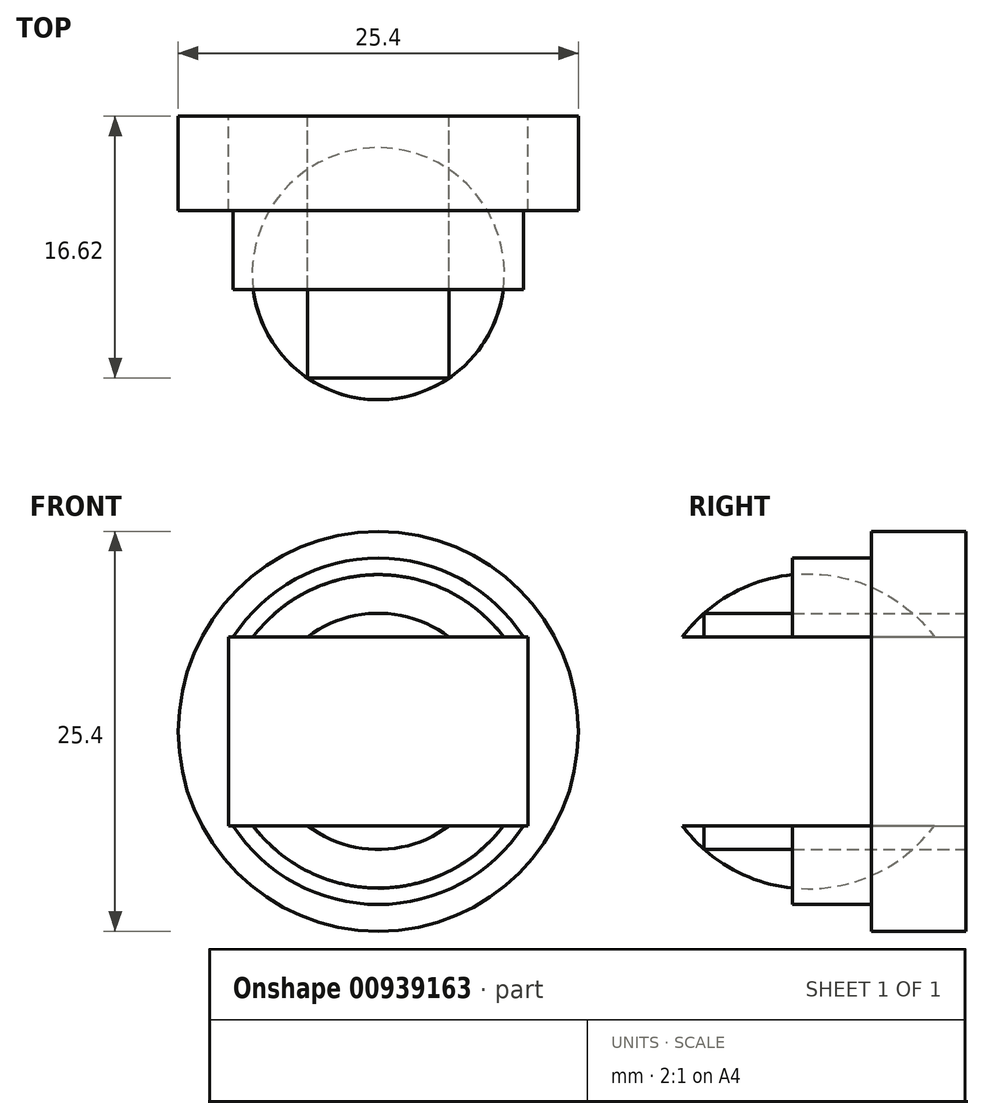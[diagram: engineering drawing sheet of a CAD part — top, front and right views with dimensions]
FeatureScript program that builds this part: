
annotation { "Feature Type Name" : "Feature", "Feature Type Description" : "" }
export const myFeature = defineFeature(function(context is Context, id is Id, definition is map)
    precondition{}
    {
        {
            var Q0;
            Q0=qCreatedBy(makeId("Front.planeOp"),FACE);
            var sketch = newSketch(context, id + "F0", { "sketchPlane" : qUnion([Q0])});
            skCircle(sketch, "E0", {"center": v(0, 0) * mm, "radius": 12.7 * mm});
            skSolve(sketch);
        }
        {
            var Q0;
            Q0=makeQuery(id+"F0.imprint","IMPRINT",FACE,{"disambiguationData":[TD([[makeQuery(id+"F0.imprint","IMPRINT",EDGE,{"derivedFrom":sQuery(id+"F0.wireOp",EDGE,"E0")}),1.0]])]});
            extrude(context, id + "F1", {"entities" : qUnion([Q0]), "depth" : 6 * mm, "offsetDistance" : 25 * mm});
        }
        {
            var Q0;
            Q0=qCreatedBy(makeId("Right.planeOp"),FACE);
            var sketch = newSketch(context, id + "F2", { "sketchPlane" : qUnion([Q0])});
            skArc(sketch, "E1", {"start": v(-10, -10) * mm, "mid": v(0, 0) * mm, "end": v(-10, 10) * mm});
            skLineSegment(sketch, "E2", {"start": v(-10, -10) * mm, "end": v(-10, 10) * mm, "construction": true});
            skLineSegment(sketch, "E3", {"start": v(-10, 10) * mm, "end": v(-10, -10) * mm});
            skSolve(sketch);
        }
        {
            var Q0;
            Q0=makeQuery(id+"F2.imprint","IMPRINT",FACE,{"disambiguationData":[TD([[makeQuery(id+"F2.imprint","IMPRINT",EDGE,{"derivedFrom":sQuery(id+"F2.wireOp",EDGE,"E1")}),1.0]])]});
            var Q1;
            Q1=sQuery(id+"F2.wireOp",EDGE,"E3");
            revolve(context, id + "F3", {"surfaceOperationType" : NewSurfaceOperationType.ADD, "entities" : qUnion([Q0]), "axis" : qUnion([Q1]), "revolveType" : RevolveType.FULL});
        }
        {
            var Q0;
            Q0=makeQuery(id+"F1.opExtrude","CAP_FACE",FACE,{"disambiguationData":[OSD([sQuery(id+"F0.wireOp",EDGE,"E0")])],"isStart":true});
            var sketch = newSketch(context, id + "F4", { "sketchPlane" : qUnion([Q0])});
            skCircle(sketch, "E4", {"center": v(0, 0) * mm, "radius": 7.5 * mm});
            skLineSegment(sketch, "E5.bottom", {"start": v(-9.5, 6) * mm, "end": v(9.5, 6) * mm});
            skLineSegment(sketch, "E5.top", {"start": v(-9.5, -6) * mm, "end": v(9.5, -6) * mm});
            skLineSegment(sketch, "E5.left", {"start": v(-9.5, 6) * mm, "end": v(-9.5, -6) * mm});
            skLineSegment(sketch, "E5.right", {"start": v(9.5, 6) * mm, "end": v(9.5, -6) * mm});
            skSolve(sketch);
        }
        {
            var Q0;
            {var subQ0=sQuery(id+"F4.wireOp",EDGE,"E5.bottom");var subQ1=sQuery(id+"F4.wireOp",EDGE,"E4");var subQ2=makeQuery(id+"F4.imprint","INTERSECT",VERTEX,{"disambiguationData":[OD(0.0)],"derivedFrom":[subQ1,subQ0]});Q0=makeQuery(id+"F4.imprint","IMPRINT",FACE,{"disambiguationData":[TD([[makeQuery(id+"F4.imprint","IMPRINT",EDGE,{"disambiguationData":[TD([[subQ2,1.0]])],"derivedFrom":subQ1}),1.0]])]});}
            var Q1;
            {var subQ0=sQuery(id+"F4.wireOp",EDGE,"E5.top");var subQ1=sQuery(id+"F4.wireOp",EDGE,"E4");var subQ2=makeQuery(id+"F4.imprint","INTERSECT",VERTEX,{"disambiguationData":[OD(0.0)],"derivedFrom":[subQ1,subQ0]});Q1=makeQuery(id+"F4.imprint","IMPRINT",FACE,{"disambiguationData":[TD([[makeQuery(id+"F4.imprint","IMPRINT",EDGE,{"disambiguationData":[TD([[subQ2,-1.0]])],"derivedFrom":subQ1}),1.0]])]});}
            var Q2;
            {var subQ0=sQuery(id+"F4.wireOp",EDGE,"E5.bottom");var subQ1=sQuery(id+"F4.wireOp",EDGE,"E4");var subQ2=makeQuery(id+"F4.imprint","INTERSECT",VERTEX,{"disambiguationData":[OD(0.0)],"derivedFrom":[subQ1,subQ0]});Q2=makeQuery(id+"F4.imprint","IMPRINT",FACE,{"disambiguationData":[TD([[makeQuery(id+"F4.imprint","IMPRINT",EDGE,{"disambiguationData":[TD([[subQ2,-1.0]])],"derivedFrom":subQ1}),1.0]])]});}
            var Q3;
            {var subQ5=sQuery(id+"F4.wireOp",EDGE,"E5.right");Q3=makeQuery(id+"F4.imprint","IMPRINT",FACE,{"disambiguationData":[TD([[makeQuery(id+"F4.imprint","IMPRINT",EDGE,{"derivedFrom":subQ5}),-1.0]])]});}
            var Q4;
            {var subQ5=sQuery(id+"F4.wireOp",EDGE,"E5.left");Q4=makeQuery(id+"F4.imprint","IMPRINT",FACE,{"disambiguationData":[TD([[makeQuery(id+"F4.imprint","IMPRINT",EDGE,{"derivedFrom":subQ5}),1.0]])]});}
            extrude(context, id + "F5", {"entities" : qUnion([Q0, Q1, Q2, Q3, Q4]), "operationType" : NewBodyOperationType.REMOVE, "oppositeDirection" : true, "depth" : 25 * mm, "offsetDistance" : 25 * mm});
        }
        {
            var Q0;
            Q0=makeQuery(id+"F1.opExtrude","CAP_FACE",FACE,{"disambiguationData":[OSD([sQuery(id+"F0.wireOp",EDGE,"E0")])],"isStart":false});
            var sketch = newSketch(context, id + "F6", { "sketchPlane" : qUnion([Q0])});
            skCircle(sketch, "E6", {"center": v(0, 0) * mm, "radius": 11 * mm});
            skSolve(sketch);
        }
        {
            var Q0;
            {var subQ1=sQuery(id+"F4.wireOp",EDGE,"E5.bottom");var subQ2=sQuery(id+"F4.wireOp",EDGE,"E4");var subQ3=makeQuery(id+"F4.imprint","INTERSECT",VERTEX,{"disambiguationData":[OD(0.0)],"derivedFrom":[subQ2,subQ1]});var subQ4=makeQuery(id+"F1.opExtrude","CAP_FACE",FACE,{"disambiguationData":[OSD([sQuery(id+"F0.wireOp",EDGE,"E0")])],"isStart":false});var subQ10=makeQuery(id+"F5.boolean.opBoolean","INTERSECT",EDGE,{"derivedFrom":[subQ4,makeQuery(id+"F5.opExtrude","SWEPT_FACE",FACE,{"disambiguationData":[OSD([subQ2]),TDD([makeQuery(id+"F4.imprint","IMPRINT",EDGE,{"disambiguationData":[TD([[subQ3,1.0]])],"derivedFrom":subQ2})])]})]});Q0=makeQuery(id+"F6.imprint","IMPRINT",FACE,{"disambiguationData":[TD([[makeQuery(id+"F6.imprint","IMPRINT",EDGE,{"derivedFrom":subQ10}),-1.0]])]});}
            var Q1;
            {var subQ1=sQuery(id+"F4.wireOp",EDGE,"E5.top");var subQ2=sQuery(id+"F4.wireOp",EDGE,"E4");var subQ4=makeQuery(id+"F1.opExtrude","CAP_FACE",FACE,{"disambiguationData":[OSD([sQuery(id+"F0.wireOp",EDGE,"E0")])],"isStart":false});var subQ7=makeQuery(id+"F4.imprint","INTERSECT",VERTEX,{"disambiguationData":[OD(0.0)],"derivedFrom":[subQ2,subQ1]});var subQ10=makeQuery(id+"F5.boolean.opBoolean","INTERSECT",EDGE,{"derivedFrom":[subQ4,makeQuery(id+"F5.opExtrude","SWEPT_FACE",FACE,{"disambiguationData":[OSD([subQ2]),TDD([makeQuery(id+"F4.imprint","IMPRINT",EDGE,{"disambiguationData":[TD([[subQ7,-1.0]])],"derivedFrom":subQ2})])]})]});Q1=makeQuery(id+"F6.imprint","IMPRINT",FACE,{"disambiguationData":[TD([[makeQuery(id+"F6.imprint","IMPRINT",EDGE,{"derivedFrom":subQ10}),-1.0]])]});}
            extrude(context, id + "F7", {"entities" : qUnion([Q0, Q1]), "operationType" : NewBodyOperationType.ADD, "depth" : 5 * mm, "offsetDistance" : 25 * mm});
        }
        {
            var Q0;
            Q0=makeQuery(id+"F3.opRevolve","SWEPT_BODY",BODY,{"disambiguationData":[OSD([sQuery(id+"F2.wireOp",EDGE,"E1"),sQuery(id+"F2.wireOp",EDGE,"E3")])]});
            var Q1;
            Q1=makeQuery(id+"F1.opExtrude","SWEPT_BODY",BODY,{"disambiguationData":[OSD([sQuery(id+"F0.wireOp",EDGE,"E0")])]});
            booleanBodies(context, id + "F8", {"operationType" : BooleanOperationType.SUBTRACTION, "tools" : qUnion([Q0]), "targets" : qUnion([Q1])});
        }
    });
